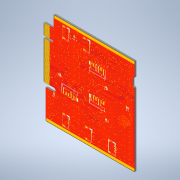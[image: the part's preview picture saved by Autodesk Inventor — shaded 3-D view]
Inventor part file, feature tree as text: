
AUTODESK INVENTOR PART (.ipt)
format: ipt  version: 2021 (Build 250183000, 183)  size: 2,015,232 bytes
history: native  units: in
note: dims shown in document units (in); Inventor stores cm internally (conversion verified against a paired STEP export)
features: sketch x6, other x4, projected_geometry x3, extrude x2, chamfer x1, fillet x1, plane x1, hole x1
ambient origin geometry x8: Origin, YZ Plane, XZ Plane, XY Plane, X Axis, Y Axis, Z Axis, Center Point
bodies: Solid1 (feature_tree)
feature tree (19):
  extrude  "Extrusion1"  Depth=3.7717in
  chamfer  "Chamfer1"  Distance=0.063in
  fillet  "Fillet1"  Radius=3.7795in
  extrude  "Extrusion6"  Depth=0.0039in
  plane  "Work Plane1"
  sketch  "Sketch17"  dims[d3=0.3937in d4=0.063in d5=0.0in d20=3.7795in]
  sketch  "Sketch18"  dims[d21=3.7795in d22=0.0039in]
  other  "Decal3"
  other  "Decal4"
  hole  "Hole10"  [1 undecoded]
  sketch  "Sketch16"  dims[d0=2.0197in d1=3.7717in]
  projected_geometry  "Projected Loop5"
  projected_geometry  "Projected Loop6"
  projected_geometry  "Projected Loop7"
  sketch  "Sketch19"  dims[d23=0.0039in d24=0.0787in]
  sketch  "Sketch20"  dims[d25=0.0039in]
  other  "Image7"
  other  "Image8"
  sketch  "Sketch22"  dims[d28=0.4429in d29=2.2047in d31=0.374in d32=1.2008in d34=0.1378in d35=0.4783in d36=1.5413in d37=0.5709in d38=0.0453in d39=0.0709in d40=2.7559in d42=0.0709in d43=1.9685in d45=0.0709in d48=0.0787in d49=0.1339in d50=0.0748in d51=0.3307in d52=0.9449in d53=0.0197in d54=0.0787in d55=45.0deg d56=0.0197in d145=0.0394in d146=1.1417in d147=0.315in d148=1.3386in d149=0.3937in d150=0.0in d151=0.1575in d152=1.5748in d154=0.0394in d155=1.5748in d157=0.0394in d160=1.6535in d161=0.0394in d162=0.7874in d164=0.0394in d165=9.8425in d167=0.0394in d170=0.0197in d171=0.1181in d172=0.0197in d173=0.3937in d174=2.7559in d176=0.0394in d177=1.5748in d179=0.0394in d197=0.0118in d198=0.315in d199=0.0118in d200=0.0787in d201=90.0deg d202=0.315in d203=0.8108in]
note: 1 required parameter value undecoded (feature->parameter linkage not recoverable at this tier; creation-order binding heuristic only, values carry confidence <= 0.55)
